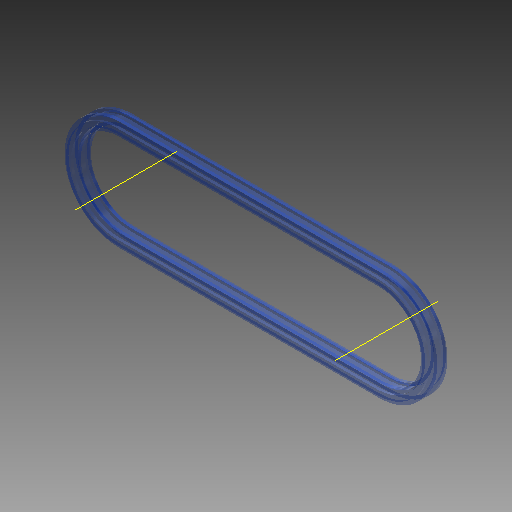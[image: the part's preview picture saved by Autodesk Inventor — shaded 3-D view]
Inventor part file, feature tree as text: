
AUTODESK INVENTOR PART (.ipt)
format: ipt  version: 2017 (Build 210142000, 142)  size: 174,080 bytes
history: native  units: mm
features: other x5, plane x2, pattern_linear x1
ambient origin geometry x8: Origin, YZ Plane, XZ Plane, XY Plane, X Axis, Y Axis, Z Axis, Center Point
bodies: Solid1 (feature_tree), Solid (feature_tree)
feature tree (8):
  other  "Work Axis1"
  other  "Work Axis2"
  plane  "Work Plane2"
  plane  "Work Plane3"
  other  "Path"
  other  "Section Plane"
  pattern_linear  "Strand Pattern"  Spacing1=0.0mm  [1 undecoded]
  other  "Section Sketch"
note: 1 required parameter value undecoded (feature->parameter linkage not recoverable at this tier; creation-order binding heuristic only, values carry confidence <= 0.55)
